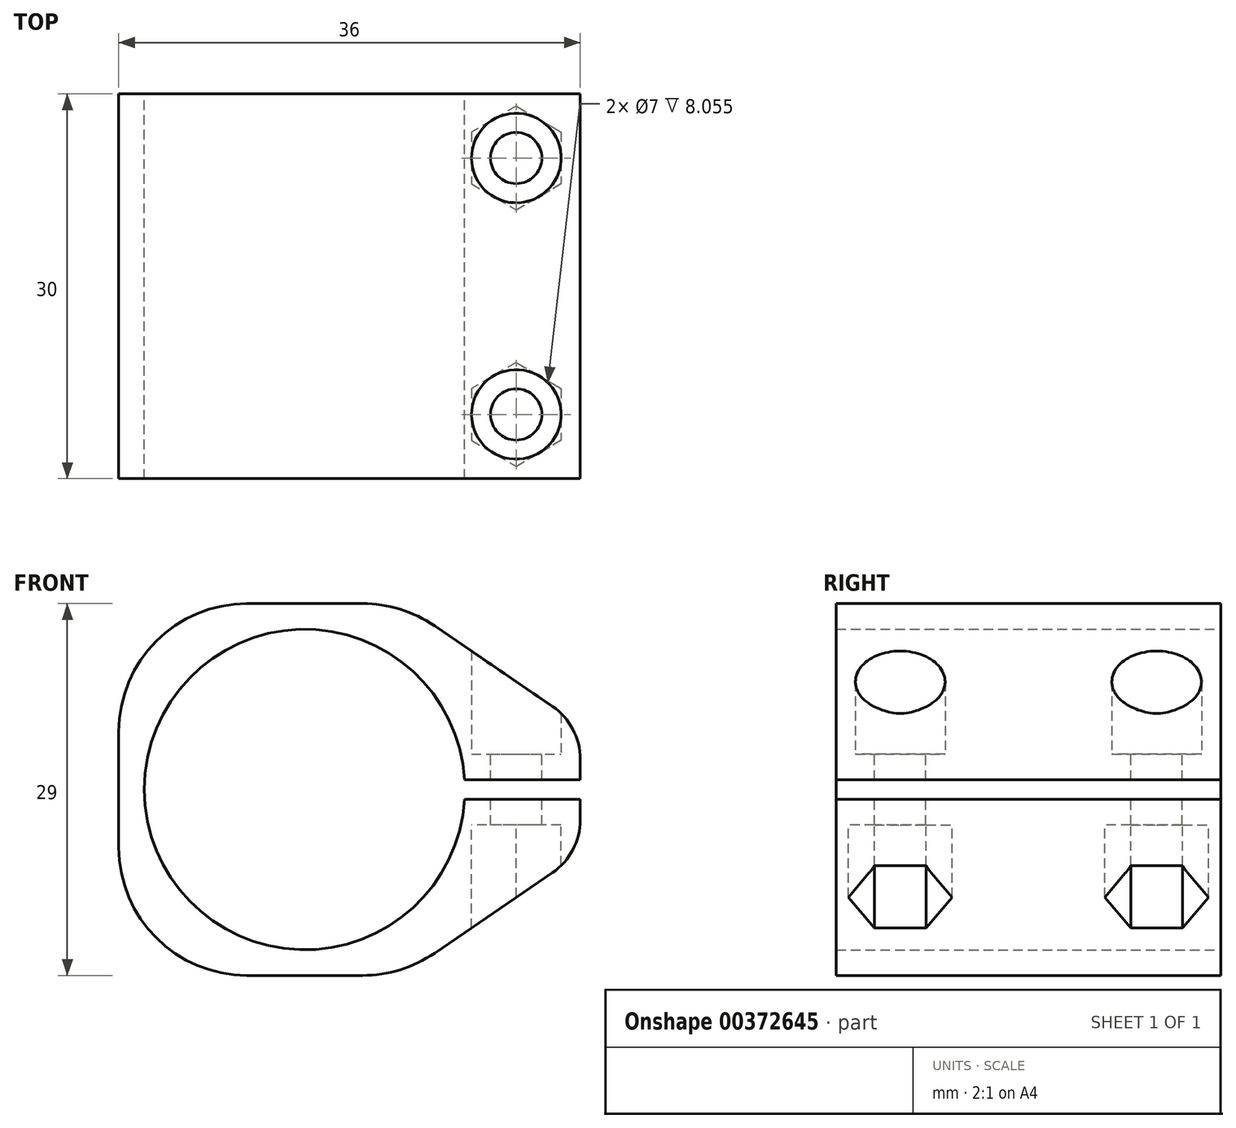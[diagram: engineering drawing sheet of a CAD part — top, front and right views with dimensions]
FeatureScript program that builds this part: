
annotation { "Feature Type Name" : "Feature", "Feature Type Description" : "" }
export const myFeature = defineFeature(function(context is Context, id is Id, definition is map)
    precondition{}
    {
        {
            var Q0;
            Q0=qCreatedBy(makeId("Front.planeOp"),FACE);
            var sketch = newSketch(context, id + "F0", { "sketchPlane" : qUnion([Q0])});
            skArc(sketch, "E0", {"start": v(12.48, 0.75) * mm, "mid": v(-12.5, 0) * mm, "end": v(12.48, -0.75) * mm});
            skLineSegment(sketch, "E1.bottom", {"start": v(14.5, 5) * mm, "end": v(18.5, 5) * mm, "construction": true});
            skLineSegment(sketch, "E1.top", {"start": v(14.5, -5) * mm, "end": v(18.5, -5) * mm, "construction": true});
            skLineSegment(sketch, "E1.left", {"start": v(14.5, 5) * mm, "end": v(14.5, -5) * mm, "construction": true});
            skLineSegment(sketch, "E1.right", {"start": v(18.5, 5) * mm, "end": v(18.5, -5) * mm, "construction": true});
            skLineSegment(sketch, "E2", {"start": v(0, 0) * mm, "end": v(14.5, 0) * mm, "construction": true});
            skLineSegment(sketch, "E3", {"start": v(21.5, -5) * mm, "end": v(21.5, -0.75) * mm});
            skLineSegment(sketch, "E4", {"start": v(21.5, 5) * mm, "end": v(10.14, 12.76) * mm});
            skLineSegment(sketch, "E5", {"start": v(21.5, -5) * mm, "end": v(10.14, -12.76) * mm});
            skLineSegment(sketch, "E6", {"start": v(12.48, 0.75) * mm, "end": v(21.5, 0.75) * mm});
            skLineSegment(sketch, "E7", {"start": v(12.48, -0.75) * mm, "end": v(21.5, -0.75) * mm});
            skLineSegment(sketch, "E8.trimOffspring", {"start": v(21.5, 0.75) * mm, "end": v(21.5, 5) * mm});
            skLineSegment(sketch, "E9", {"start": v(12.48, 0.75) * mm, "end": v(12.48, 0) * mm, "construction": true});
            skLineSegment(sketch, "E10", {"start": v(12.48, 0) * mm, "end": v(12.48, -0.75) * mm, "construction": true});
            skLineSegment(sketch, "E11.bottom", {"start": v(-4.5, 14.5) * mm, "end": v(4.5, 14.5) * mm});
            skLineSegment(sketch, "E11.top", {"start": v(-4.5, -14.5) * mm, "end": v(4.5, -14.5) * mm});
            skLineSegment(sketch, "E11.left", {"start": v(-14.5, 4.5) * mm, "end": v(-14.5, -4.5) * mm});
            skPoint(sketch, "E12.visualSharp", {"position": v(-14.5, 14.5) * mm});
            skArc(sketch, "E12.filletArc", {"start": v(-4.5, 14.5) * mm, "mid": v(-11.57, 11.57) * mm, "end": v(-14.5, 4.5) * mm});
            skPoint(sketch, "E13.visualSharp", {"position": v(-14.5, -14.5) * mm});
            skArc(sketch, "E13.filletArc", {"start": v(-14.5, -4.5) * mm, "mid": v(-11.57, -11.57) * mm, "end": v(-4.5, -14.5) * mm});
            skPoint(sketch, "E14.visualSharp", {"position": v(14.5, -14.5) * mm});
            skArc(sketch, "E14.filletArc", {"start": v(4.5, -14.5) * mm, "mid": v(7.45, -14.05) * mm, "end": v(10.14, -12.76) * mm});
            skPoint(sketch, "E15.visualSharp", {"position": v(14.5, 14.5) * mm});
            skArc(sketch, "E15.filletArc", {"start": v(10.14, 12.76) * mm, "mid": v(7.45, 14.05) * mm, "end": v(4.5, 14.5) * mm});
            skSolve(sketch);
        }
        {
            var Q0;
            Q0=makeQuery(id+"F0.imprint","IMPRINT",FACE,{"disambiguationData":[TD([[makeQuery(id+"F0.imprint","IMPRINT",EDGE,{"derivedFrom":sQuery(id+"F0.wireOp",EDGE,"E0")}),-1.0]])]});
            var Q1;
            Q1=makeQuery(id+"F0.imprint","IMPRINT",FACE,{"disambiguationData":[TD([[makeQuery(id+"F0.imprint","IMPRINT",EDGE,{"derivedFrom":sQuery(id+"F0.wireOp",EDGE,"E3")}),1.0]])]});
            extrude(context, id + "F1", {"entities" : qUnion([Q0, Q1]), "depth" : 30 * mm, "offsetDistance" : 25 * mm, "symmetric" : true});
        }
        {
            var Q0;
            Q0=qCreatedBy(makeId("Top.planeOp"),FACE);
            var sketch = newSketch(context, id + "F2", { "sketchPlane" : qUnion([Q0])});
            skCircle(sketch, "E16", {"center": v(16.5, 10) * mm, "radius": 2 * mm});
            skCircle(sketch, "E17", {"center": v(16.5, -10) * mm, "radius": 2 * mm});
            skLineSegment(sketch, "E18", {"start": v(16.5, 10) * mm, "end": v(16.5, -10) * mm, "construction": true});
            skLineSegment(sketch, "E19", {"start": v(0, 0) * mm, "end": v(16.5, 0) * mm, "construction": true});
            skSolve(sketch);
        }
        {
            var Q0;
            Q0 = qSketchRegion(id + "F2", true);
            extrude(context, id + "F3", {"entities" : qUnion([Q0]), "operationType" : NewBodyOperationType.REMOVE, "endBound" : BoundingType.THROUGH_ALL, "oppositeDirection" : true, "depth" : 25 * mm, "offsetDistance" : 25 * mm, "hasSecondDirection" : true, "secondDirectionBound" : BoundingType.THROUGH_ALL, "secondDirectionOppositeDirection" : false, "secondDirectionDepth" : 25 * mm});
        }
        {
            var Q0;
            Q0=makeQuery(id+"F1.opExtrude","SWEPT_FACE",FACE,{"disambiguationData":[OSD([sQuery(id+"F0.wireOp",EDGE,"E6")])]});
            cPlane(context, id + "F4", {"entities" : qUnion([Q0]), "cplaneType" : CPlaneType.OFFSET, "offset" : 2 * mm, "oppositeDirection" : true, "width" : 150 * mm, "height" : 150 * mm});
        }
        {
            var Q0;
            Q0=makeQuery(id+"F1.opExtrude","SWEPT_EDGE",EDGE,{"disambiguationData":[OSD([sQuery(id+"F0.wireOp",EDGE,"E4"),sQuery(id+"F0.wireOp",EDGE,"E8.trimOffspring")])]});
            var Q1;
            Q1=makeQuery(id+"F1.opExtrude","SWEPT_EDGE",EDGE,{"disambiguationData":[OSD([sQuery(id+"F0.wireOp",EDGE,"E3"),sQuery(id+"F0.wireOp",EDGE,"E5")])]});
            fillet(context, id + "F5", {"entities" : qUnion([Q0, Q1]), "radius" : 5 * mm, "tangentPropagation" : true, "allowEdgeOverflow" : false});
        }
        {
            var Q0;
            Q0=qCreatedBy(id+"F4.planeOp",FACE);
            var sketch = newSketch(context, id + "F6", { "sketchPlane" : qUnion([Q0])});
            skCircle(sketch, "E20", {"center": v(16.5, 10) * mm, "radius": 3.5 * mm});
            skCircle(sketch, "E21", {"center": v(16.5, -10) * mm, "radius": 3.5 * mm});
            skSolve(sketch);
        }
        {
            var Q0;
            Q0 = qSketchRegion(id + "F6", true);
            extrude(context, id + "F7", {"entities" : qUnion([Q0]), "operationType" : NewBodyOperationType.REMOVE, "endBound" : BoundingType.THROUGH_ALL, "oppositeDirection" : true, "depth" : 25 * mm, "offsetDistance" : 25 * mm});
        }
        {
            var Q0;
            Q0=makeQuery(id+"F1.opExtrude","SWEPT_FACE",FACE,{"disambiguationData":[OSD([sQuery(id+"F0.wireOp",EDGE,"E7")])]});
            cPlane(context, id + "F8", {"entities" : qUnion([Q0]), "cplaneType" : CPlaneType.OFFSET, "offset" : 2 * mm, "oppositeDirection" : true, "width" : 150 * mm, "height" : 150 * mm});
        }
        {
            var Q0;
            Q0=qCreatedBy(id+"F8.planeOp",FACE);
            var sketch = newSketch(context, id + "F9", { "sketchPlane" : qUnion([Q0])});
            skCircle(sketch, "E22.cCircle", {"center": v(16.5, 10) * mm, "radius": 3.5 * mm, "construction": true});
            skLineSegment(sketch, "E22.0", {"start": v(20, 12.02) * mm, "end": v(20, 7.98) * mm});
            skLineSegment(sketch, "E22.1", {"start": v(20, 7.98) * mm, "end": v(16.5, 5.96) * mm});
            skLineSegment(sketch, "E22.2", {"start": v(16.5, 5.96) * mm, "end": v(13, 7.98) * mm});
            skLineSegment(sketch, "E22.3", {"start": v(13, 7.98) * mm, "end": v(13, 12.02) * mm});
            skLineSegment(sketch, "E22.4", {"start": v(13, 12.02) * mm, "end": v(16.5, 14.04) * mm});
            skLineSegment(sketch, "E22.5", {"start": v(16.5, 14.04) * mm, "end": v(20, 12.02) * mm});
            skPoint(sketch, "E22.0.midPoint", {"position": v(20, 10) * mm});
            skCircle(sketch, "E23.cCircle", {"center": v(16.5, -10) * mm, "radius": 3.5 * mm, "construction": true});
            skLineSegment(sketch, "E23.0", {"start": v(20, -7.98) * mm, "end": v(20, -12.02) * mm});
            skLineSegment(sketch, "E23.1", {"start": v(20, -12.02) * mm, "end": v(16.5, -14.04) * mm});
            skLineSegment(sketch, "E23.2", {"start": v(16.5, -14.04) * mm, "end": v(13, -12.02) * mm});
            skLineSegment(sketch, "E23.3", {"start": v(13, -12.02) * mm, "end": v(13, -7.98) * mm});
            skLineSegment(sketch, "E23.4", {"start": v(13, -7.98) * mm, "end": v(16.5, -5.96) * mm});
            skLineSegment(sketch, "E23.5", {"start": v(16.5, -5.96) * mm, "end": v(20, -7.98) * mm});
            skPoint(sketch, "E23.0.midPoint", {"position": v(20, -10) * mm});
            skSolve(sketch);
        }
        {
            var Q0;
            Q0 = qSketchRegion(id + "F9", true);
            extrude(context, id + "F10", {"entities" : qUnion([Q0]), "operationType" : NewBodyOperationType.REMOVE, "endBound" : BoundingType.THROUGH_ALL, "oppositeDirection" : true, "depth" : 25 * mm, "offsetDistance" : 25 * mm});
        }
    });
